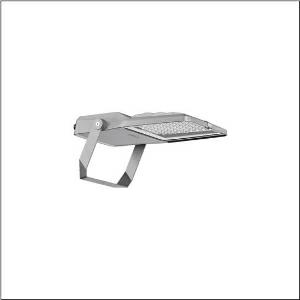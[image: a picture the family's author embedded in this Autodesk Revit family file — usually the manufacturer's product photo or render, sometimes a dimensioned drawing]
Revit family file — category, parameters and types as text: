
# Revit family: floodlight_fl_21_mini___pl64_5xa7776b2e1a_6c25
name_source: partatom
category: Lighting Fixtures
units: mm (PartAtom-declared; Revit-internal decimal feet)

## family parameters
Cut with Voids When Loaded = No
Host = Face
Light Source = No
Part Type = Normal
Room Calculation Point = No
Round Connector Dimension = Use Diameter
Shared = No

## types (1)
- --- (1 x LED, 6010 lm, 45.7 W, 3000K)
    Apparent Load = 46 VA
    CIE Flux Codes = 28 80 98 100 100
    Color Rendering = 70
    Color Temperature = 3000K
    Default Elevation = 1800 mm
    Description = Floodlight FL 21 mini, floodlight, primary light control with lens, of PMMA, primary optical cover: protective disc, of toughened safety glass, transparent, light distribution: PL64, light emission: direct distribution, installation type: surface-mounted, LED, High Power LED, rated luminous flux: 6.010lm, luminous efficacy: 132lm/W, light colour: 730, colour temperature: 3000K, control gear: Smart Interface (Zhaga), control: flexible luminous flux parameterisation, time-dependent luminous flux control, constant luminous flux control, overheat protection, pre-setting: logarithmic dimming characteristic, with terminal, 6-pole, mains connection: 220..240V, AC, 50/60Hz, start of lifetime: 46W, end of service life: 48W, reduction: 22W, luminaire housing, of diecast aluminium, powder-coated, Siteco® metallic grey (DB 702S), corrosivity category C5 mid according to DIN EN ISO 12944, suitable for swimming pools, chlorine-resistant, sealing non-destructively replaceable, mounting bracket, of steel, galvanised, powder-coated, Siteco® metallic grey (DB 702S), Smart Interface below and above, protection rating (complete): IP66, insulation class (complete): insulation class II (safety insulation), certification: CE, ENEC, VDE, protection symbol: D, impact resistance: IK08, permissible operating ambient temperature: -40..+40°C, permissible operating ambient temperature for outdoor applications: -40..+50°C, standard: DIN EN 12944, LABS conformity tested according to VDMA 24364:2018-05, packaging unit: 1 piece

Light Distribution: PL64
    Height = 70 mm
    Lamp = 1 x LED
    Lamp Light Flux = 6010 lm
    Lamp Power = 45.7 W
    Lamp count = 1
    Length = 485 mm
    Luminous efficacy = 132 lm/W
    Manufacturer = Siteco
    ModVariant = No
    Model = 5XA7776B2E1A
    Number of Poles = 1
    OnlyDefault = Yes
    Power Factor = 1
    Product Name = Floodlight FL 21 mini | PL64
    Product group = floodlight | pylon annexe
    ProductGroupID = 6200
    Protection Class = Protection class II
    Protection Degree = IP 66
    RLX_Detail_Level = 1
    RLX_Emergency_Light_Flux = 0 lm
    RLX_Emergency_Type = 0
    RLX_Emergency_Type_DB = No
    RlxData = <blob elided: 96021 chars, md5=402d34c1>
    Socket = socket
    Standby Power = 0 W
    System Light Flux = 6010 lm
    System Power = 46 W
    Type Comments = factory setting: luminous flux: 100 % | dim-lin: 254 | 463 mA
    Type Image = l_1006845.jpg
    URL = http://relux.com
    VarID = @adj_165510
    Voltage = 0 V
    Weight = 0.00 kg
    Width = 337 mm

## geometry (parser evidence)
native form markers: Blend x4, Sweep x13
no freeform markers — native parametric forms only
